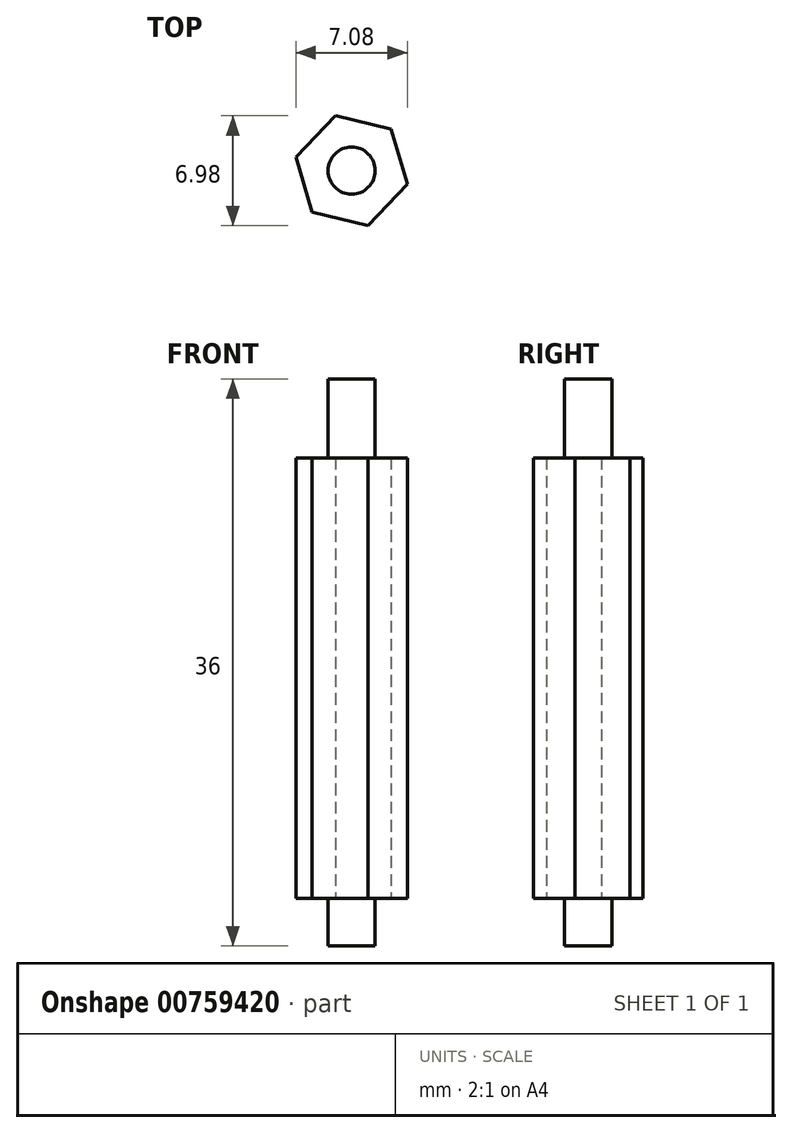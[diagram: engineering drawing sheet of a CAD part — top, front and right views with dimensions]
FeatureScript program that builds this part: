
annotation { "Feature Type Name" : "Feature", "Feature Type Description" : "" }
export const myFeature = defineFeature(function(context is Context, id is Id, definition is map)
    precondition{}
    {
        {
            var Q0;
            Q0=qCreatedBy(makeId("Top.planeOp"),FACE);
            var sketch = newSketch(context, id + "F0", { "sketchPlane" : qUnion([Q0])});
            skCircle(sketch, "E0.cCircle", {"center": v(0, 0) * mm, "radius": 3.15 * mm, "construction": true});
            skLineSegment(sketch, "E0.0", {"start": v(2.5, 2.64) * mm, "end": v(3.54, -0.85) * mm});
            skLineSegment(sketch, "E0.1", {"start": v(3.54, -0.85) * mm, "end": v(1.03, -3.49) * mm});
            skLineSegment(sketch, "E0.2", {"start": v(1.03, -3.49) * mm, "end": v(-2.5, -2.64) * mm});
            skLineSegment(sketch, "E0.3", {"start": v(-2.5, -2.64) * mm, "end": v(-3.54, 0.85) * mm});
            skLineSegment(sketch, "E0.4", {"start": v(-3.54, 0.85) * mm, "end": v(-1.03, 3.49) * mm});
            skLineSegment(sketch, "E0.5", {"start": v(-1.03, 3.49) * mm, "end": v(2.5, 2.64) * mm});
            skPoint(sketch, "E0.0.midPoint", {"position": v(3.02, 0.9) * mm});
            skSolve(sketch);
        }
        {
            var Q0;
            Q0 = qSketchRegion(id + "F0", true);
            extrude(context, id + "F1", {"entities" : qUnion([Q0]), "depth" : 28 * mm, "offsetDistance" : 25 * mm});
        }
        {
            var Q0;
            Q0=makeQuery(id+"F1.opExtrude","CAP_FACE",FACE,{"disambiguationData":[OSD([sQuery(id+"F0.wireOp",EDGE,"E0.0"),sQuery(id+"F0.wireOp",EDGE,"E0.1"),sQuery(id+"F0.wireOp",EDGE,"E0.2"),sQuery(id+"F0.wireOp",EDGE,"E0.3"),sQuery(id+"F0.wireOp",EDGE,"E0.4"),sQuery(id+"F0.wireOp",EDGE,"E0.5")])],"isStart":false});
            var sketch = newSketch(context, id + "F2", { "sketchPlane" : qUnion([Q0])});
            skCircle(sketch, "E1", {"center": v(0, 0) * mm, "radius": 1.5 * mm});
            skSolve(sketch);
        }
        {
            var Q0;
            Q0 = qSketchRegion(id + "F2", true);
            extrude(context, id + "F3", {"entities" : qUnion([Q0]), "operationType" : NewBodyOperationType.ADD, "depth" : 5 * mm, "offsetDistance" : 25 * mm});
        }
        {
            var Q0;
            Q0=makeQuery(id+"F1.opExtrude","CAP_FACE",FACE,{"disambiguationData":[OSD([sQuery(id+"F0.wireOp",EDGE,"E0.0"),sQuery(id+"F0.wireOp",EDGE,"E0.1"),sQuery(id+"F0.wireOp",EDGE,"E0.2"),sQuery(id+"F0.wireOp",EDGE,"E0.3"),sQuery(id+"F0.wireOp",EDGE,"E0.4"),sQuery(id+"F0.wireOp",EDGE,"E0.5")])],"isStart":true});
            var sketch = newSketch(context, id + "F4", { "sketchPlane" : qUnion([Q0])});
            skCircle(sketch, "E2", {"center": v(0, 0) * mm, "radius": 1.5 * mm});
            skSolve(sketch);
        }
        {
            var Q0;
            Q0 = qSketchRegion(id + "F4", true);
            extrude(context, id + "F5", {"entities" : qUnion([Q0]), "operationType" : NewBodyOperationType.ADD, "depth" : 3 * mm, "offsetDistance" : 25 * mm});
        }
    });
